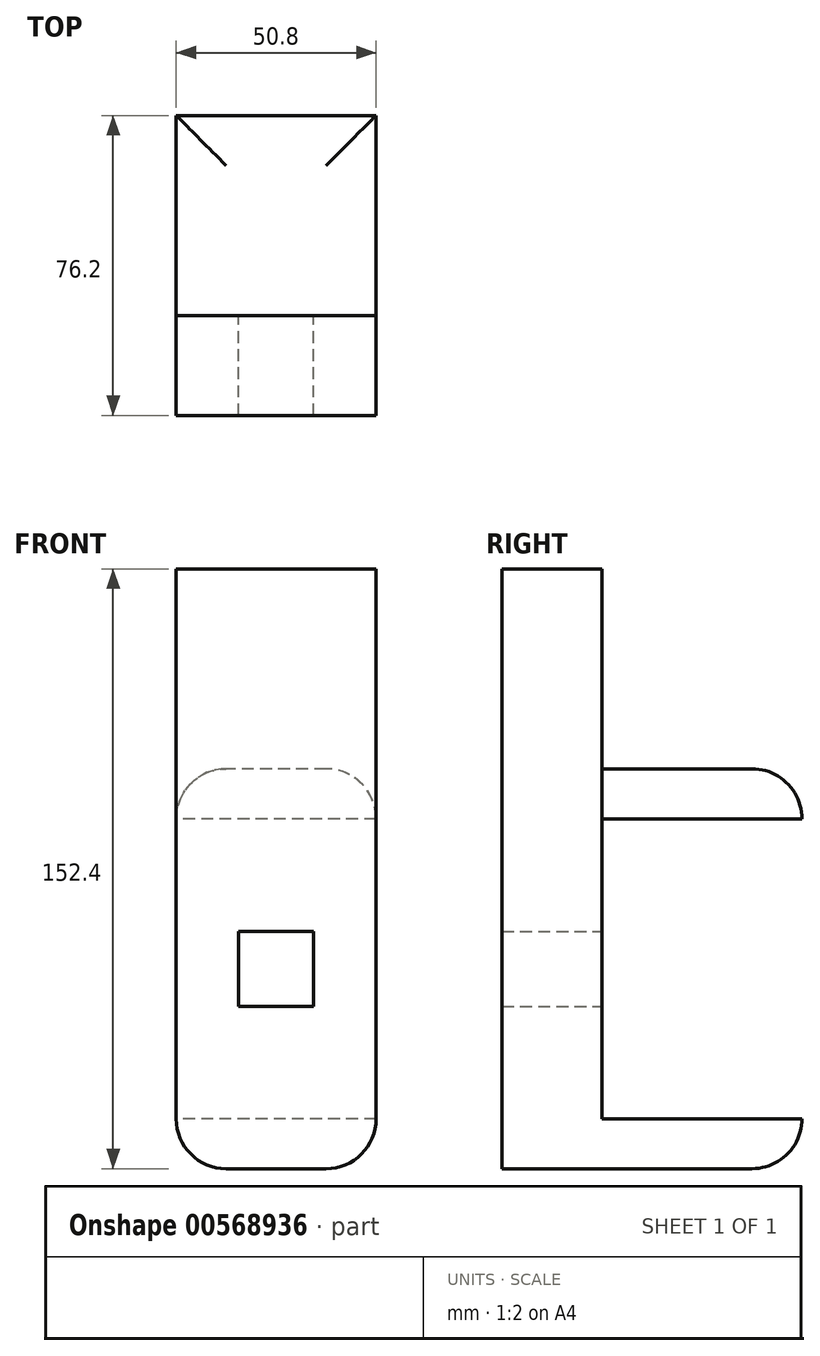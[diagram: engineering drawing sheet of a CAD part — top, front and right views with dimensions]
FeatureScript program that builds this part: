
annotation { "Feature Type Name" : "Feature", "Feature Type Description" : "" }
export const myFeature = defineFeature(function(context is Context, id is Id, definition is map)
    precondition{}
    {
        {
            var Q0;
            Q0=qCreatedBy(makeId("Front.planeOp"),FACE);
            var sketch = newSketch(context, id + "F0", { "sketchPlane" : qUnion([Q0])});
            skLineSegment(sketch, "E0.bottom", {"start": v(25.4, 50.8) * mm, "end": v(-25.4, 50.8) * mm});
            skLineSegment(sketch, "E0.top", {"start": v(25.4, -50.8) * mm, "end": v(-25.4, -50.8) * mm});
            skLineSegment(sketch, "E0.left", {"start": v(25.4, 50.8) * mm, "end": v(25.4, -50.8) * mm});
            skLineSegment(sketch, "E0.right", {"start": v(-25.4, 50.8) * mm, "end": v(-25.4, -50.8) * mm});
            skPoint(sketch, "E0.middle", {"position": v(0, 0) * mm});
            skLineSegment(sketch, "E1.bottom", {"start": v(-9.53, 9.54) * mm, "end": v(9.52, 9.54) * mm});
            skLineSegment(sketch, "E1.top", {"start": v(-9.53, -9.51) * mm, "end": v(9.52, -9.51) * mm});
            skLineSegment(sketch, "E1.left", {"start": v(-9.53, 9.54) * mm, "end": v(-9.53, -9.51) * mm});
            skLineSegment(sketch, "E1.right", {"start": v(9.52, 9.54) * mm, "end": v(9.52, -9.51) * mm});
            skSolve(sketch);
        }
        {
            var Q0;
            Q0 = qSketchRegion(id + "F0", true);
            extrude(context, id + "F1", {"entities" : qUnion([Q0]), "depth" : 25.4 * mm, "offsetDistance" : 25.4 * mm, "symmetric" : true});
        }
        {
            var Q0;
            Q0=makeQuery(id+"F1.opExtrude","CAP_FACE",FACE,{"disambiguationData":[OSD([sQuery(id+"F0.wireOp",EDGE,"E0.bottom"),sQuery(id+"F0.wireOp",EDGE,"E0.top"),sQuery(id+"F0.wireOp",EDGE,"E0.left"),sQuery(id+"F0.wireOp",EDGE,"E0.right")])],"isStart":true});
            var sketch = newSketch(context, id + "F2", { "sketchPlane" : qUnion([Q0])});
            skLineSegment(sketch, "E2.bottom", {"start": v(-25.4, 50.8) * mm, "end": v(25.4, 50.8) * mm});
            skLineSegment(sketch, "E2.top", {"start": v(-25.4, 38.1) * mm, "end": v(25.4, 38.1) * mm});
            skLineSegment(sketch, "E2.left", {"start": v(-25.4, 50.8) * mm, "end": v(-25.4, 38.1) * mm});
            skLineSegment(sketch, "E2.right", {"start": v(25.4, 50.8) * mm, "end": v(25.4, 38.1) * mm});
            skLineSegment(sketch, "E3.bottom", {"start": v(-25.4, -50.8) * mm, "end": v(25.4, -50.8) * mm});
            skLineSegment(sketch, "E3.top", {"start": v(-25.4, -38.1) * mm, "end": v(25.4, -38.1) * mm});
            skLineSegment(sketch, "E3.left", {"start": v(-25.4, -50.8) * mm, "end": v(-25.4, -38.1) * mm});
            skLineSegment(sketch, "E3.right", {"start": v(25.4, -50.8) * mm, "end": v(25.4, -38.1) * mm});
            skLineSegment(sketch, "E4.top", {"start": v(-25.4, 101.6) * mm, "end": v(25.4, 101.6) * mm});
            skLineSegment(sketch, "E4.left", {"start": v(-25.4, 50.8) * mm, "end": v(-25.4, 101.6) * mm});
            skLineSegment(sketch, "E4.right", {"start": v(25.4, 50.8) * mm, "end": v(25.4, 101.6) * mm});
            skSolve(sketch);
        }
        {
            var Q0;
            Q0=makeQuery(id+"F2.imprint","IMPRINT",FACE,{"disambiguationData":[TD([[makeQuery(id+"F2.imprint","IMPRINT",EDGE,{"derivedFrom":sQuery(id+"F2.wireOp",EDGE,"E3.bottom")}),1.0]])]});
            var Q1;
            Q1=makeQuery(id+"F2.imprint","IMPRINT",FACE,{"disambiguationData":[TD([[makeQuery(id+"F2.imprint","IMPRINT",EDGE,{"derivedFrom":sQuery(id+"F2.wireOp",EDGE,"E2.top")}),1.0]])]});
            extrude(context, id + "F3", {"entities" : qUnion([Q0, Q1]), "operationType" : NewBodyOperationType.ADD, "depth" : 50.8 * mm, "offsetDistance" : 25.4 * mm});
        }
        {
            var Q0;
            Q0=makeQuery(id+"F2.imprint","IMPRINT",FACE,{"disambiguationData":[TD([[makeQuery(id+"F2.imprint","IMPRINT",EDGE,{"derivedFrom":sQuery(id+"F2.wireOp",EDGE,"E2.bottom")}),1.0]])]});
            extrude(context, id + "F4", {"entities" : qUnion([Q0]), "operationType" : NewBodyOperationType.ADD, "oppositeDirection" : true, "depth" : 25.4 * mm, "offsetDistance" : 25.4 * mm});
        }
        {
            var Q0;
            Q0=makeQuery(id+"F3.boolean.opBoolean","MERGE",EDGE,{"derivedFrom":[makeQuery(id+"F1.opExtrude","SWEPT_EDGE",EDGE,{"disambiguationData":[OSD([sQuery(id+"F0.wireOp",EDGE,"E0.bottom"),sQuery(id+"F0.wireOp",EDGE,"E0.right")])]}),makeQuery(id+"F3.opExtrude","SWEPT_EDGE",EDGE,{"disambiguationData":[OSD([sQuery(id+"F2.wireOp",EDGE,"E2.right"),sQuery(id+"F2.wireOp",EDGE,"E2.bottom"),sQuery(id+"F2.wireOp",EDGE,"E4.right")])]})]});
            var Q1;
            Q1=makeQuery(id+"F3.boolean.opBoolean","MERGE",EDGE,{"derivedFrom":[makeQuery(id+"F1.opExtrude","SWEPT_EDGE",EDGE,{"disambiguationData":[OSD([sQuery(id+"F0.wireOp",EDGE,"E0.bottom"),sQuery(id+"F0.wireOp",EDGE,"E0.left")])]}),makeQuery(id+"F3.opExtrude","SWEPT_EDGE",EDGE,{"disambiguationData":[OSD([sQuery(id+"F2.wireOp",EDGE,"E2.left"),sQuery(id+"F2.wireOp",EDGE,"E2.bottom"),sQuery(id+"F2.wireOp",EDGE,"E4.left")])]})]});
            var Q2;
            Q2=makeQuery(id+"F3.opExtrude","CAP_EDGE",EDGE,{"disambiguationData":[OSD([sQuery(id+"F2.wireOp",EDGE,"E2.bottom")])],"isStart":false});
            var Q3;
            Q3=makeQuery(id+"F3.boolean.opBoolean","MERGE",EDGE,{"derivedFrom":[makeQuery(id+"F1.opExtrude","SWEPT_EDGE",EDGE,{"disambiguationData":[OSD([sQuery(id+"F0.wireOp",EDGE,"E0.top"),sQuery(id+"F0.wireOp",EDGE,"E0.right")])]}),makeQuery(id+"F3.opExtrude","SWEPT_EDGE",EDGE,{"disambiguationData":[OSD([sQuery(id+"F2.wireOp",EDGE,"E3.bottom"),sQuery(id+"F2.wireOp",EDGE,"E3.right")])]})]});
            var Q4;
            Q4=makeQuery(id+"F3.opExtrude","CAP_EDGE",EDGE,{"disambiguationData":[OSD([sQuery(id+"F2.wireOp",EDGE,"E3.bottom")])],"isStart":false});
            var Q5;
            Q5=makeQuery(id+"F3.boolean.opBoolean","MERGE",EDGE,{"derivedFrom":[makeQuery(id+"F1.opExtrude","SWEPT_EDGE",EDGE,{"disambiguationData":[OSD([sQuery(id+"F0.wireOp",EDGE,"E0.top"),sQuery(id+"F0.wireOp",EDGE,"E0.left")])]}),makeQuery(id+"F3.opExtrude","SWEPT_EDGE",EDGE,{"disambiguationData":[OSD([sQuery(id+"F2.wireOp",EDGE,"E3.bottom"),sQuery(id+"F2.wireOp",EDGE,"E3.left")])]})]});
            fillet(context, id + "F5", {"entities" : qUnion([Q0, Q1, Q2, Q3, Q4, Q5]), "radius" : 12.7 * mm, "tangentPropagation" : true, "allowEdgeOverflow" : false});
        }
    });
